# Revit family: EKF_EE_МонтажнаяПлатаДляГоризонтальныхАвтоматическихВыключателейTrivia_AVERES
name_source: partatom
category: Электрооборудование
units: mm (PartAtom-declared; Revit-internal decimal feet)

## family parameters
Всегда вертикально = Нет
На основе рабочей плоскости = Да
Общий = Да
При загрузке вырезать с полостями = Нет
Размер круглого соединителя = Использовать диаметр
Тип детали = Силовой щит
Точка расчета площади = Нет

## types (12) — shared parameters
ADSK_Единица измерения = шт.
ADSK_Завод-изготовитель = EKF
ADSK_Количество = 1
ADSK_Материал = RAL 7035_Сталь
ADSK_Размер_Глубина = 18 мм
Изготовитель = EKF
Отметка по умолчанию = 1219.2 мм
Серия номенклатуры = Averes
Степень защиты IP = -
ТВ = EKF_2_TRIVIA_AVERES
Тип установки = -
Тип_Платы = Монтажная плата 1
zero-valued in all types: ADSK_Масса

## per-type parameters (varying)
| type | ADSK_Код изделия | ADSK_Марка | ADSK_Наименование | ADSK_Обозначение | ADSK_Размер_Высота | ADSK_Размер_Ширина | Тип |
| Монтажная плата для горизонтального  AV POWER-4 TM/ ETU 3/4Р | MPFU0501 | Монтажная плата для горизонтального AV POWER-4 TM/ ETU 3/4Р | Монтажная плата для горизонтального AV POWER-4 TM/ ETU 3/4Р | Монтажная плата для горизонтального AV POWER-4 TM/ ETU 3/4Р | 348 мм | 515 мм | 542 мм |
| Монтажная плата для горизонтального AV POWER-1 ETU  3/4P | MPFU0201 | Монтажная плата для горизонтального AV POWER-1 ETU 3/4P | Монтажная плата для горизонтального AV POWER-1 ETU 3/4P | Монтажная плата для горизонтального AV POWER-1 ETU 3/4P | 198 мм | 515 мм | 543 мм |
| Монтажная плата для горизонтального AV POWER-1 TM 3/4P | MPFU0101 | Монтажная плата для горизонтального AV POWER-1 TM 3/4P | Монтажная плата для горизонтального AV POWER-1 TM 3/4P | Монтажная плата для горизонтального AV POWER-1 TM 3/4P | 148 мм | 514 мм | 544 мм |
| Монтажная плата для горизонтального AV POWER-2 TM/ETU 3/4P EKF AVERES | MPFU0301 | Монтажная плата для горизонтального AV POWER-2 TM/ETU 3/4P EKF AVERES | Монтажная плата для горизонтального AV POWER-2 TM/ETU 3/4P EKF AVERES | Монтажная плата для горизонтального AV POWER-2 TM/ETU 3/4P EKF AVERES | 198 мм | 515 мм | 545 мм |
| Монтажная плата для горизонтального AV POWER-3 TM/ETU 3/4P EKF AVERES | MPFU0401 | Монтажная плата для горизонтального AV POWER-3 TM/ETU 3/4P EKF AVERES | Монтажная плата для горизонтального AV POWER-3 TM/ETU 3/4P EKF AVERES | Монтажная плата для горизонтального AV POWER-3 TM/ETU 3/4P EKF AVERES | 248 мм | 515 мм | 546 мм |
| Монтажная плата для горизонтального ВА-99/125 3Р/4P EKF AVERES | MPFU2101 | Монтажная плата для горизонтального ВА-99/125 3Р/4P EKF AVERES | Монтажная плата для горизонтального ВА-99/125 3Р/4P EKF AVERES | Монтажная плата для горизонтального ВА-99/125 3Р/4P EKF AVERES | 148 мм | 515 мм | 547 мм |
| Монтажная плата для горизонтального ВА-99/160 3Р/4Р | MPFU2201 | Монтажная плата для горизонтального ВА-99/160 3Р/4Р | Монтажная плата для горизонтального ВА-99/160 3Р/4Р | Монтажная плата для горизонтального ВА-99/160 3Р/4Р | 198 мм | 515 мм | 548 мм |
| Монтажная плата для горизонтального ВА-99/250 3Р/4P EKF AVERES | MPFU2301 | Монтажная плата для горизонтального ВА-99/250 3Р/4P EKF AVERES | Монтажная плата для горизонтального ВА-99/250 3Р/4P EKF AVERES | Монтажная плата для горизонтального ВА-99/250 3Р/4P EKF AVERES | 198 мм | 515 мм | 549 мм |
| Монтажная плата для горизонтального ВА-99/400 3Р/4P EKF AVERES | MPFU2401 | Монтажная плата для горизонтального ВА-99/400 3Р/4P EKF AVERES | Монтажная плата для горизонтального ВА-99/400 3Р/4P EKF AVERES | Монтажная плата для горизонтального ВА-99/400 3Р/4P EKF AVERES | 248 мм | 515 мм | 550 мм |
| Монтажная плата для горизонтального ВА-99/800 3Р/4P EKF AVERES | MPFU2501 | Монтажная плата для горизонтального ВА-99/800 3Р/4P EKF AVERES | Монтажная плата для горизонтального ВА-99/800 3Р/4P EKF AVERES | Монтажная плата для горизонтального ВА-99/800 3Р/4P EKF AVERES | 348 мм | 515 мм | 551 мм |
| Монтажная плата для горизонтального ВА-99С/400/630 3Р/4Р EKF AVERES | MPFU6301 | Монтажная плата для горизонтального ВА-99С/400/630 3Р/4Р EKF AVERES | Монтажная плата для горизонтального ВА-99С/400/630 3Р/4Р EKF AVERES | Монтажная плата для горизонтального ВА-99С/400/630 3Р/4Р EKF AVERES | 248 мм | 515 мм | 552 мм |
| Плата монтажная для горизонтального ВА-99С/100/160/250 3Р/4Р | MPFU6201 | Плата монтажная для горизонтального ВА-99С/100/160/250 3Р/4Р | Плата монтажная для горизонтального ВА-99С/100/160/250 3Р/4Р | Плата монтажная для горизонтального ВА-99С/100/160/250 3Р/4Р | 198 мм | 515 мм | 561 мм |
